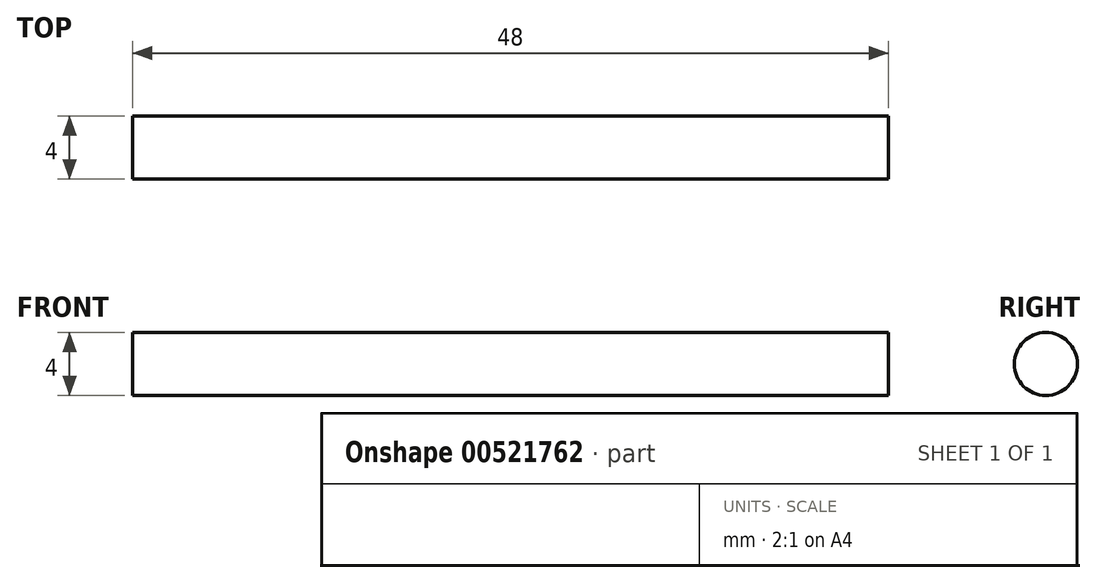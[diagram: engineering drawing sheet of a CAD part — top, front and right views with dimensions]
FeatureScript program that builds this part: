
annotation { "Feature Type Name" : "Feature", "Feature Type Description" : "" }
export const myFeature = defineFeature(function(context is Context, id is Id, definition is map)
    precondition{}
    {
        {
            var Q0;
            Q0=qCreatedBy(makeId("Right.planeOp"),FACE);
            var sketch = newSketch(context, id + "F0", { "sketchPlane" : qUnion([Q0])});
            skCircle(sketch, "E0", {"center": v(0, 0) * mm, "radius": 2 * mm});
            skSolve(sketch);
        }
        {
            var Q0;
            Q0 = qSketchRegion(id + "F0", true);
            extrude(context, id + "F1", {"entities" : qUnion([Q0]), "depth" : 48 * mm, "offsetDistance" : 25 * mm});
        }
    });
